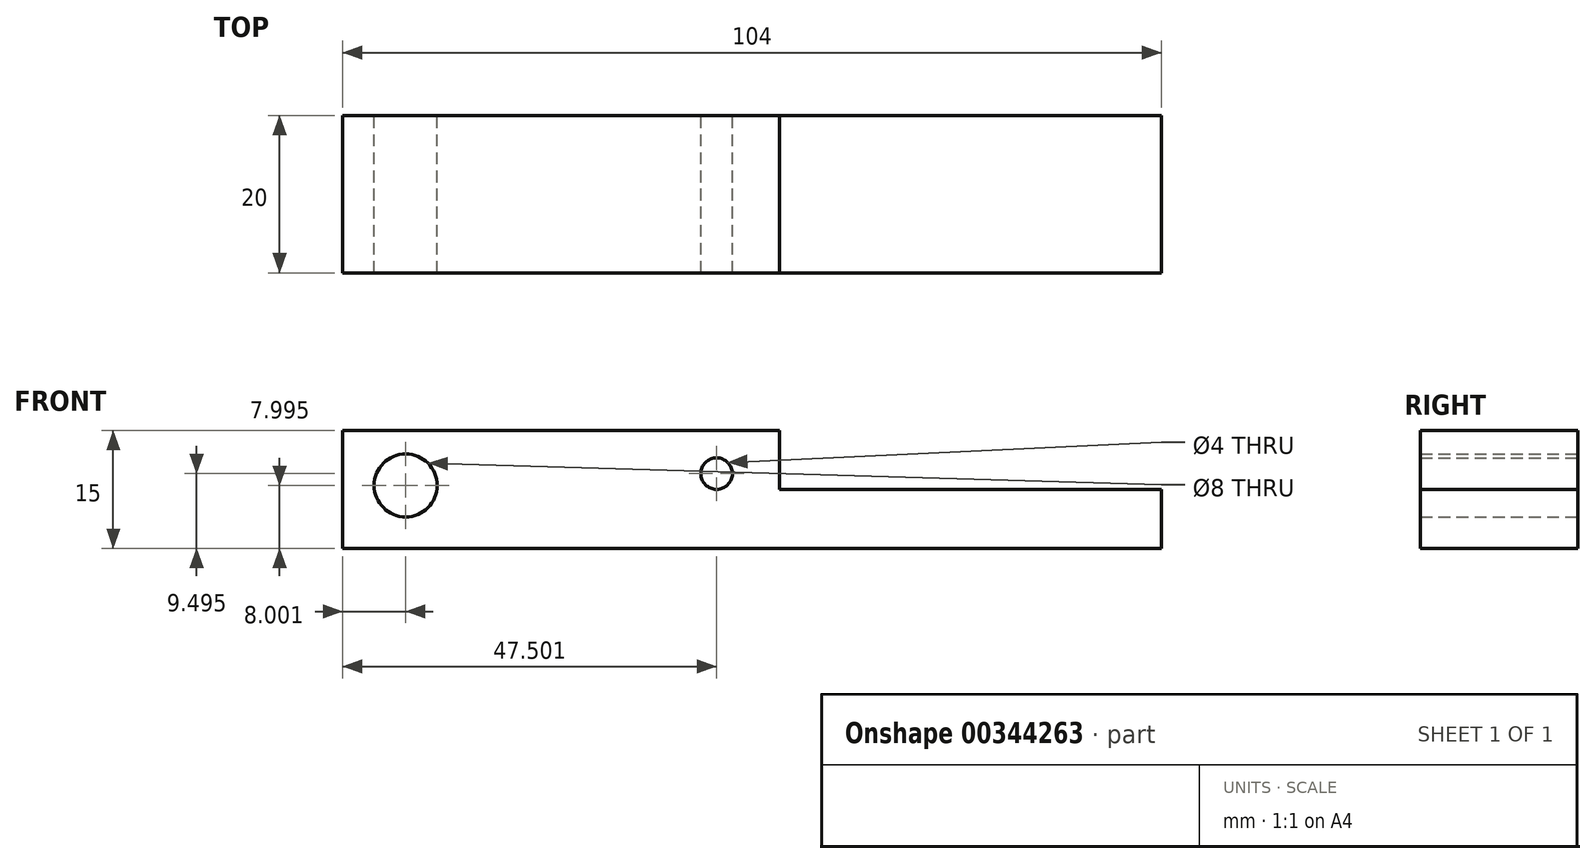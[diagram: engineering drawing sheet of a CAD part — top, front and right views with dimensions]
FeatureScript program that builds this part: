
annotation { "Feature Type Name" : "Feature", "Feature Type Description" : "" }
export const myFeature = defineFeature(function(context is Context, id is Id, definition is map)
    precondition{}
    {
        {
            var Q0;
            Q0=qCreatedBy(makeId("Front.planeOp"),FACE);
            var sketch = newSketch(context, id + "F0", { "sketchPlane" : qUnion([Q0])});
            skLineSegment(sketch, "E0", {"start": v(-17.7, -3.76) * mm, "end": v(86.3, -3.76) * mm});
            skLineSegment(sketch, "E1", {"start": v(86.3, -3.76) * mm, "end": v(86.3, 3.74) * mm});
            skLineSegment(sketch, "E2", {"start": v(86.3, 3.74) * mm, "end": v(37.8, 3.74) * mm});
            skLineSegment(sketch, "E3", {"start": v(37.8, 3.74) * mm, "end": v(37.8, 11.24) * mm});
            skLineSegment(sketch, "E4", {"start": v(-17.7, -3.76) * mm, "end": v(-17.7, 11.24) * mm});
            skLineSegment(sketch, "E5", {"start": v(37.8, 11.24) * mm, "end": v(-17.7, 11.24) * mm});
            skSolve(sketch);
        }
        {
            var Q0;
            Q0 = qSketchRegion(id + "F0", true);
            extrude(context, id + "F1", {"entities" : qUnion([Q0]), "endBound" : BoundingType.SYMMETRIC, "depth" : 20 * mm});
        }
        {
            var Q0;
            Q0=qCreatedBy(makeId("Front.planeOp"),FACE);
            var sketch = newSketch(context, id + "F2", { "sketchPlane" : qUnion([Q0])});
            skLineSegment(sketch, "E6", {"start": v(-9.7, 15.1) * mm, "end": v(-9.7, -10.72) * mm});
            skLineSegment(sketch, "E7", {"start": v(-24.88, 4.24) * mm, "end": v(-2.77, 4.24) * mm});
            skLineSegment(sketch, "E8", {"start": v(29.8, 16.04) * mm, "end": v(29.8, -11.42) * mm});
            skLineSegment(sketch, "E9", {"start": v(22.82, 5.74) * mm, "end": v(42.36, 5.74) * mm});
            skCircle(sketch, "E10", {"center": v(29.8, 5.74) * mm, "radius": 2 * mm});
            skCircle(sketch, "E11", {"center": v(-9.7, 4.24) * mm, "radius": 4 * mm});
            skSolve(sketch);
        }
        {
            var Q0;
            Q0 = qSketchRegion(id + "F2", true);
            extrude(context, id + "F3", {"entities" : qUnion([Q0]), "operationType" : NewBodyOperationType.REMOVE, "endBound" : BoundingType.SYMMETRIC, "depth" : 30 * mm});
        }
    });
